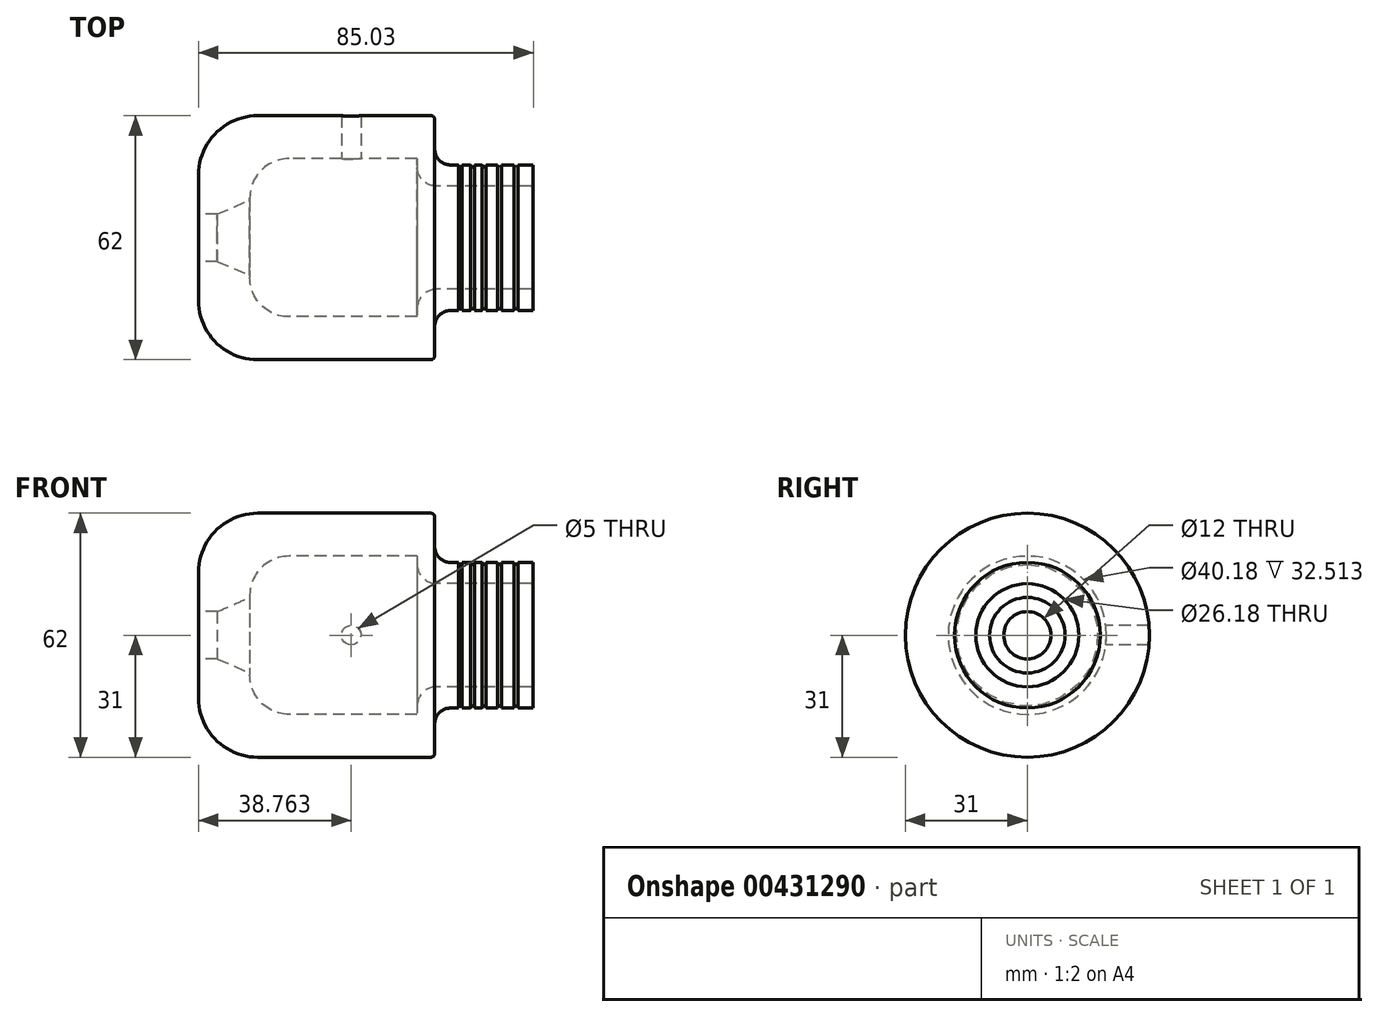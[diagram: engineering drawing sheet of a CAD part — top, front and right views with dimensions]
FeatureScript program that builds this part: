
annotation { "Feature Type Name" : "Feature", "Feature Type Description" : "" }
export const myFeature = defineFeature(function(context is Context, id is Id, definition is map)
    precondition{}
    {
        {
            var Q0;
            Q0=qCreatedBy(makeId("Front.planeOp"),FACE);
            var sketch = newSketch(context, id + "F0", { "sketchPlane" : qUnion([Q0])});
            skLineSegment(sketch, "E0.bottom", {"start": v(15, 31) * mm, "end": v(59, 31) * mm});
            skLineSegment(sketch, "E0.left", {"start": v(0, 16) * mm, "end": v(0, 6) * mm});
            skLineSegment(sketch, "E0.right", {"start": v(60, 30) * mm, "end": v(60, 22.5) * mm});
            skLineSegment(sketch, "E1", {"start": v(0, 0) * mm, "end": v(79.05, 0) * mm});
            skLineSegment(sketch, "E2.bottom", {"start": v(64, 18.5) * mm, "end": v(66, 18.5) * mm});
            skPoint(sketch, "E3.visualSharp", {"position": v(0, 31) * mm});
            skArc(sketch, "E3.filletArc", {"start": v(15, 31) * mm, "mid": v(4.4, 26.6) * mm, "end": v(0, 16) * mm});
            skLineSegment(sketch, "E4.bottom", {"start": v(23, 20.09) * mm, "end": v(55.52, 20.09) * mm});
            skLineSegment(sketch, "E4.right", {"start": v(55.52, 20.09) * mm, "end": v(55.52, 18.09) * mm});
            skLineSegment(sketch, "E5.bottom", {"start": v(60.52, 13.09) * mm, "end": v(84.53, 13.09) * mm});
            skLineSegment(sketch, "E5.top", {"start": v(85, 6.1) * mm, "end": v(85.07, 6.1) * mm});
            skPoint(sketch, "E6.visualSharp", {"position": v(13.52, 20.09) * mm});
            skArc(sketch, "E6.filletArc", {"start": v(23, 20.09) * mm, "mid": v(15.76, 16.98) * mm, "end": v(13.02, 9.59) * mm});
            skPoint(sketch, "E7.visualSharp", {"position": v(55.52, 13.09) * mm});
            skArc(sketch, "E7.filletArc", {"start": v(55.52, 18.09) * mm, "mid": v(56.98, 14.55) * mm, "end": v(60.52, 13.09) * mm});
            skLineSegment(sketch, "E8.trimOffspring", {"start": v(85, 6.1) * mm, "end": v(85, 6) * mm});
            skLineSegment(sketch, "E9", {"start": v(85, 18.5) * mm, "end": v(85.03, 13.6) * mm});
            skPoint(sketch, "E10.visualSharp", {"position": v(60, 18.5) * mm});
            skArc(sketch, "E10.filletArc", {"start": v(60, 22.5) * mm, "mid": v(61.17, 19.67) * mm, "end": v(64, 18.5) * mm});
            skPoint(sketch, "E11.visualSharp", {"position": v(60, 31) * mm});
            skArc(sketch, "E11.filletArc", {"start": v(60, 30) * mm, "mid": v(59.7, 30.7) * mm, "end": v(59, 31) * mm});
            skLineSegment(sketch, "E12", {"start": v(0, 6) * mm, "end": v(4.74, 6) * mm});
            skLineSegment(sketch, "E13", {"start": v(4.74, 6) * mm, "end": v(13.02, 9.59) * mm});
            skArc(sketch, "E14", {"start": v(66, 18.5) * mm, "mid": v(66.5, 18) * mm, "end": v(67, 18.5) * mm});
            skArc(sketch, "E15", {"start": v(69.14, 18.5) * mm, "mid": v(69.64, 18) * mm, "end": v(70.14, 18.5) * mm});
            skArc(sketch, "E16", {"start": v(72.06, 18.5) * mm, "mid": v(72.56, 18) * mm, "end": v(73.06, 18.5) * mm});
            skArc(sketch, "E17", {"start": v(75.95, 18.5) * mm, "mid": v(76.45, 18) * mm, "end": v(76.95, 18.5) * mm});
            skArc(sketch, "E18", {"start": v(80.15, 18.5) * mm, "mid": v(80.65, 18) * mm, "end": v(81.15, 18.5) * mm});
            skLineSegment(sketch, "E19.trimOffspring", {"start": v(67, 18.5) * mm, "end": v(69.14, 18.5) * mm});
            skLineSegment(sketch, "E20.trimOffspring", {"start": v(70.14, 18.5) * mm, "end": v(72.06, 18.5) * mm});
            skLineSegment(sketch, "E21.trimOffspring", {"start": v(73.06, 18.5) * mm, "end": v(75.95, 18.5) * mm});
            skLineSegment(sketch, "E22.trimOffspring", {"start": v(76.95, 18.5) * mm, "end": v(80.15, 18.5) * mm});
            skLineSegment(sketch, "E23.trimOffspring", {"start": v(81.15, 18.5) * mm, "end": v(85, 18.5) * mm});
            skArc(sketch, "E24.filletArc", {"start": v(84.53, 13.09) * mm, "mid": v(84.88, 13.24) * mm, "end": v(85.03, 13.6) * mm});
            skSolve(sketch);
        }
        {
            var Q0;
            Q0=makeQuery(id+"F0.imprint","IMPRINT",FACE,{"disambiguationData":[TD([[makeQuery(id+"F0.imprint","IMPRINT",EDGE,{"derivedFrom":sQuery(id+"F0.wireOp",EDGE,"E0.bottom")}),-1.0]])]});
            var Q1;
            Q1=sQuery(id+"F0.wireOp",EDGE,"E1");
            revolve(context, id + "F1", {"entities" : qUnion([Q0]), "axis" : qUnion([Q1]), "revolveType" : RevolveType.FULL});
        }
        {
            var Q0;
            Q0=qCreatedBy(makeId("Front.planeOp"),FACE);
            var sketch = newSketch(context, id + "F2", { "sketchPlane" : qUnion([Q0])});
            skCircle(sketch, "E25", {"center": v(38.76, 0) * mm, "radius": 2.5 * mm});
            skSolve(sketch);
        }
        {
            var Q0;
            Q0=qSketchRegion(id+"F2",true);
            var Q1;
            Q1=sQuery(id+"F2.wireOp",EDGE,"E25");
            extrude(context, id + "F3", {"entities" : qUnion([Q0]), "operationType" : NewBodyOperationType.REMOVE, "surfaceEntities" : qUnion([Q1]), "endBound" : BoundingType.THROUGH_ALL, "oppositeDirection" : true, "depth" : 60 * mm});
        }
    });
